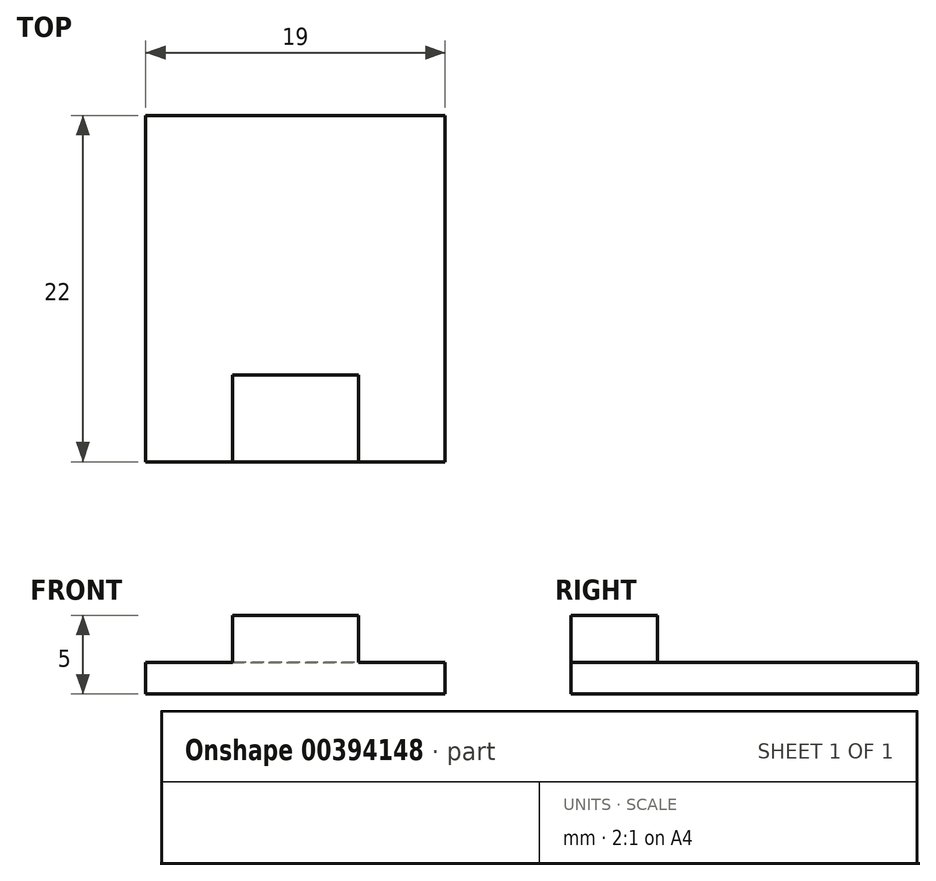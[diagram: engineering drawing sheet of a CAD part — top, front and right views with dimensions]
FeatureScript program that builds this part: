
annotation { "Feature Type Name" : "Feature", "Feature Type Description" : "" }
export const myFeature = defineFeature(function(context is Context, id is Id, definition is map)
    precondition{}
    {
        {
            var Q0;
            Q0=qCreatedBy(makeId("Top.planeOp"),FACE);
            var sketch = newSketch(context, id + "F0", { "sketchPlane" : qUnion([Q0])});
            skLineSegment(sketch, "E0.bottom", {"start": v(9.5, -11) * mm, "end": v(-9.5, -11) * mm});
            skLineSegment(sketch, "E0.top", {"start": v(9.5, 11) * mm, "end": v(-9.5, 11) * mm});
            skLineSegment(sketch, "E0.left", {"start": v(9.5, -11) * mm, "end": v(9.5, 11) * mm});
            skLineSegment(sketch, "E0.right", {"start": v(-9.5, -11) * mm, "end": v(-9.5, 11) * mm});
            skPoint(sketch, "E0.middle", {"position": v(0, 0) * mm});
            skSolve(sketch);
        }
        {
            var Q0;
            Q0=makeQuery(id+"F0.imprint","IMPRINT",FACE,{"disambiguationData":[TD([[makeQuery(id+"F0.imprint","IMPRINT",EDGE,{"derivedFrom":sQuery(id+"F0.wireOp",EDGE,"E0.bottom")}),-1.0]])]});
            extrude(context, id + "F1", {"entities" : qUnion([Q0]), "depth" : 2 * mm});
        }
        {
            var Q0;
            Q0=makeQuery(id+"F1.opExtrude","CAP_FACE",FACE,{"disambiguationData":[OSD([sQuery(id+"F0.wireOp",EDGE,"E0.bottom"),sQuery(id+"F0.wireOp",EDGE,"E0.top"),sQuery(id+"F0.wireOp",EDGE,"E0.left"),sQuery(id+"F0.wireOp",EDGE,"E0.right")])],"isStart":false});
            var sketch = newSketch(context, id + "F2", { "sketchPlane" : qUnion([Q0])});
            skLineSegment(sketch, "E1.bottom", {"start": v(0, -11) * mm, "end": v(-4, -11) * mm});
            skLineSegment(sketch, "E1.top", {"start": v(0, -5.5) * mm, "end": v(-4, -5.5) * mm});
            skLineSegment(sketch, "E1.left", {"start": v(0, -11) * mm, "end": v(0, -5.5) * mm});
            skLineSegment(sketch, "E1.right", {"start": v(-4, -11) * mm, "end": v(-4, -5.5) * mm});
            skLineSegment(sketch, "E2.MirrorCS", {"start": v(0, -5.5) * mm, "end": v(4, -5.5) * mm});
            skLineSegment(sketch, "E3.MirrorCS", {"start": v(4, -11) * mm, "end": v(4, -5.5) * mm});
            skLineSegment(sketch, "E4.MirrorCS", {"start": v(0, -11) * mm, "end": v(4, -11) * mm});
            skSolve(sketch);
        }
        {
            var Q0;
            Q0=makeQuery(id+"F2.imprint","IMPRINT",FACE,{"disambiguationData":[TD([[makeQuery(id+"F2.imprint","IMPRINT",EDGE,{"derivedFrom":sQuery(id+"F2.wireOp",EDGE,"E1.left")}),-1.0]])]});
            var Q1;
            Q1=makeQuery(id+"F2.imprint","IMPRINT",FACE,{"disambiguationData":[TD([[makeQuery(id+"F2.imprint","IMPRINT",EDGE,{"derivedFrom":sQuery(id+"F2.wireOp",EDGE,"E1.bottom")}),-1.0]])]});
            extrude(context, id + "F3", {"entities" : qUnion([Q0, Q1]), "operationType" : NewBodyOperationType.ADD, "depth" : 3 * mm});
        }
    });
